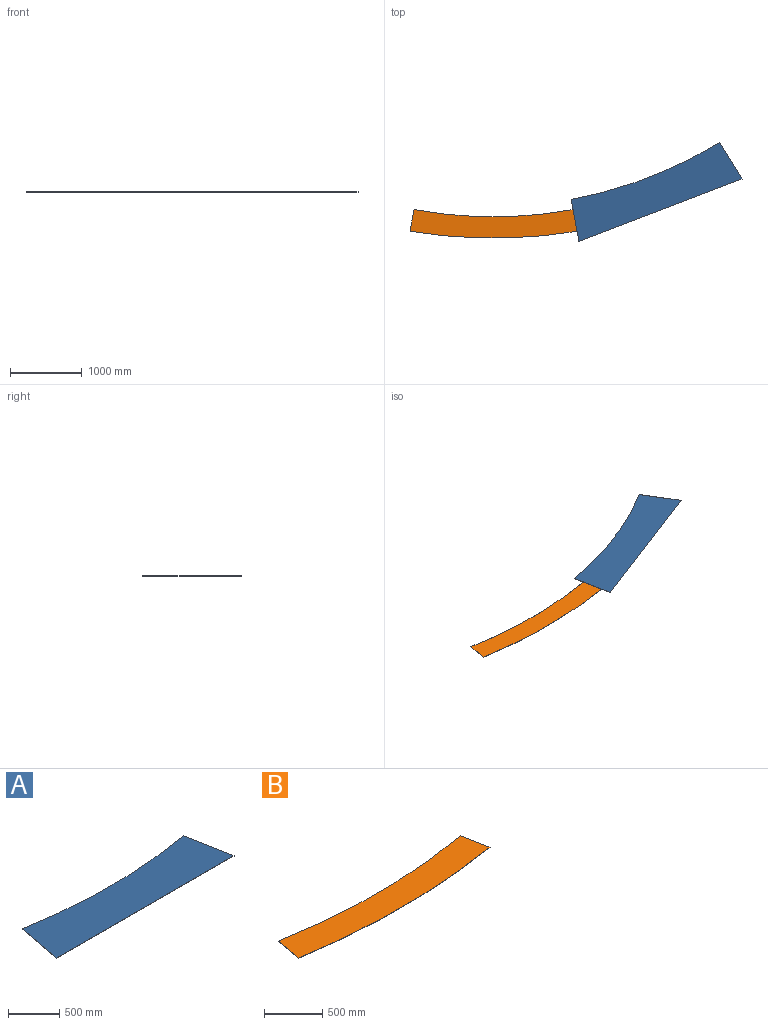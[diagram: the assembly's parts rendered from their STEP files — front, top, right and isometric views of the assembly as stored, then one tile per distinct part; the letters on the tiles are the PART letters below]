
ASSEMBLY  parts=2 mates=1
PART A: 6 faces, bbox 2438.4x588.4x3.2 mm
  f0: cylinder r=6096mm len=2220.44mm, axis (0,0,1), area 7089.5mm2, adj f1,f2,f4,f5
  f1: plane 2438.4x588.39mm, normal (0,0,1), area 1219427.4mm2, adj f0,f3,f4,f5
  f2: plane 2438.4x588.39mm, normal (0,0,-1), area 1219427.4mm2, adj f0,f3,f4,f5
  f3: plane 2438.4x3.18mm, normal (0,-1,0), area 7741.9mm2, adj f1,f2,f4,f5
  f4: plane 588.39x108.98mm, normal (-0.98,0.18,0), area 1899.9mm2, adj f0,f1,f2,f3
  f5: plane 588.39x108.98mm, normal (0.98,0.18,0), area 1899.9mm2, adj f0,f1,f2,f3
PART B: 6 faces, bbox 2332.7x397.9x3.2 mm
  f0: plane 2332.65x397.89mm, normal (0,0,1), area 686323.1mm2, adj f2,f3,f4,f5
  f1: plane 2332.65x397.89mm, normal (0,0,-1), area 686323.1mm2, adj f2,f3,f4,f5
  f2: cylinder r=6096mm len=2220.44mm, axis (0,0,1), area 7089.5mm2, adj f0,f1,f3,f4
  f3: plane 302.93x56.11mm, normal (-0.98,0.18,0), area 978.1mm2, adj f0,f1,f2,f5
  f4: plane 302.93x56.11mm, normal (0.98,0.18,0), area 978.1mm2, adj f0,f1,f2,f5
  f5: cylinder r=7210.07mm len=2332.65mm, axis (0,0,1), area 7438.9mm2, adj f0,f1,f3,f4
PLACE A rot(axis=(0,0,1),21deg) t=(2331.09,579.39,0)mm
PLACE B at identity fixed
MATE fastened B.f4 <-> A.f4  axis (0.98,0.18,0) through (1138.27,436.92,1.59)mm
